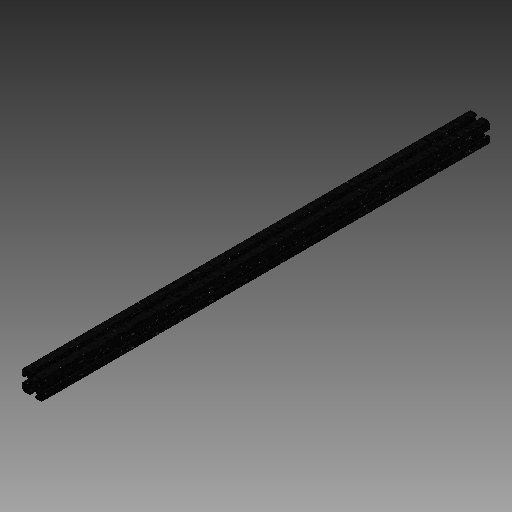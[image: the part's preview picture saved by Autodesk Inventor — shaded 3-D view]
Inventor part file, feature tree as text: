
AUTODESK INVENTOR PART (.ipt)
format: ipt  version: 2019 (Build 230136000, 136)  size: 250,368 bytes
history: native  units: in
note: dims shown in document units (in); Inventor stores cm internally (conversion verified against a paired STEP export)
features: plane x1, extrude x1, sketch x1
ambient origin geometry x8: Origin, YZ Plane, XZ Plane, XY Plane, X Axis, Y Axis, Z Axis, Center Point
bodies: Solid1 (feature_tree)
feature tree (3):
  plane  "Work Plane1"
  extrude  "Extrusion1"  [1 undecoded]
  sketch  "Sketch1"  dims[d0=12.0in d1=0.0in]
note: 1 required parameter value undecoded (feature->parameter linkage not recoverable at this tier; creation-order binding heuristic only, values carry confidence <= 0.55)
